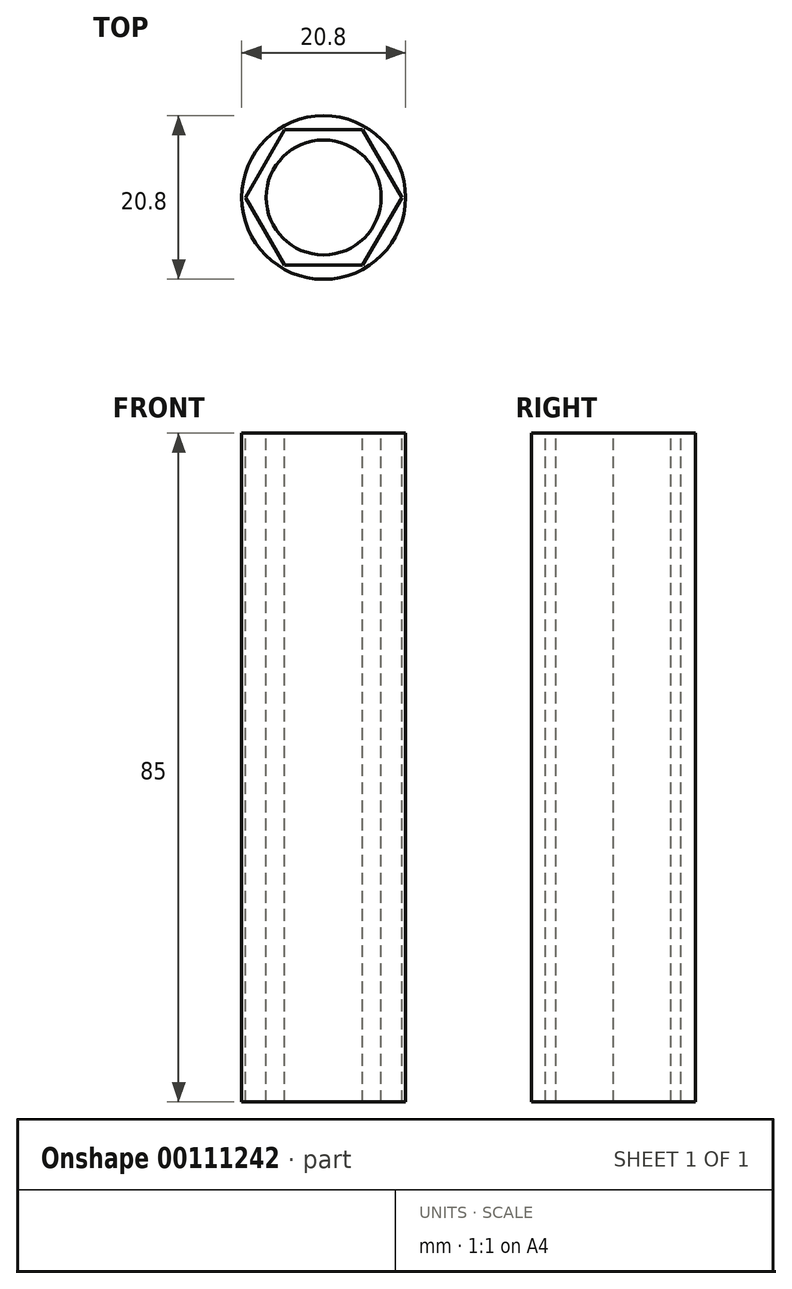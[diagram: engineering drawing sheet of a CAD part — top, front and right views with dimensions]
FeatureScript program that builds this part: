
annotation { "Feature Type Name" : "Feature", "Feature Type Description" : "" }
export const myFeature = defineFeature(function(context is Context, id is Id, definition is map)
    precondition{}
    {
        {
            var Q0;
            Q0=qCreatedBy(makeId("Top.planeOp"),FACE);
            var sketch = newSketch(context, id + "F0", { "sketchPlane" : qUnion([Q0])});
            skCircle(sketch, "E0.cCircle", {"center": v(0, 0) * mm, "radius": 8.6 * mm, "construction": true});
            skLineSegment(sketch, "E0.0", {"start": v(-4.97, 8.6) * mm, "end": v(4.97, 8.6) * mm});
            skLineSegment(sketch, "E0.1", {"start": v(4.97, 8.6) * mm, "end": v(9.93, 0) * mm});
            skLineSegment(sketch, "E0.2", {"start": v(9.93, 0) * mm, "end": v(4.97, -8.6) * mm});
            skLineSegment(sketch, "E0.3", {"start": v(4.97, -8.6) * mm, "end": v(-4.97, -8.6) * mm});
            skLineSegment(sketch, "E0.4", {"start": v(-4.97, -8.6) * mm, "end": v(-9.93, 0) * mm});
            skLineSegment(sketch, "E0.5", {"start": v(-9.93, 0) * mm, "end": v(-4.97, 8.6) * mm});
            skPoint(sketch, "E0.0.midPoint", {"position": v(0, 8.6) * mm});
            skSolve(sketch);
        }
        {
            var Q0;
            Q0=qCreatedBy(makeId("Top.planeOp"),FACE);
            var sketch = newSketch(context, id + "F1", { "sketchPlane" : qUnion([Q0])});
            skCircle(sketch, "E1", {"center": v(0, 0) * mm, "radius": 10.4 * mm});
            skSolve(sketch);
        }
        {
            var Q0;
            Q0=qCreatedBy(makeId("Top.planeOp"),FACE);
            var sketch = newSketch(context, id + "F2", { "sketchPlane" : qUnion([Q0])});
            skCircle(sketch, "E2", {"center": v(0, 0) * mm, "radius": 7.3 * mm});
            skSolve(sketch);
        }
        {
            var Q0;
            Q0=qCreatedBy(makeId("Top.planeOp"),FACE);
            cPlane(context, id + "F3", {"entities" : qUnion([Q0]), "cplaneType" : CPlaneType.OFFSET, "offset" : 85 * mm, "oppositeDirection" : true, "width" : 150 * mm, "height" : 150 * mm});
        }
        {
            var Q0;
            Q0 = qSketchRegion(id + "F0", true);
            var Q1;
            Q1=qCreatedBy(id+"F3.planeOp",FACE);
            extrude(context, id + "F4", {"entities" : qUnion([Q0]), "endBound" : BoundingType.UP_TO_SURFACE, "oppositeDirection" : true, "endBoundEntityFace" : qUnion([Q1]), "depth" : 25 * mm});
        }
        {
            var Q0;
            Q0 = qSketchRegion(id + "F1", true);
            var Q1;
            Q1=qCreatedBy(id+"F3.planeOp",FACE);
            extrude(context, id + "F5", {"entities" : qUnion([Q0]), "endBound" : BoundingType.UP_TO_SURFACE, "oppositeDirection" : true, "endBoundEntityFace" : qUnion([Q1]), "depth" : 25 * mm});
        }
        {
            var Q0;
            Q0 = qSketchRegion(id + "F2", true);
            var Q1;
            Q1=qCreatedBy(id+"F3.planeOp",FACE);
            extrude(context, id + "F6", {"entities" : qUnion([Q0]), "endBound" : BoundingType.UP_TO_SURFACE, "oppositeDirection" : true, "endBoundEntityFace" : qUnion([Q1]), "depth" : 25 * mm});
        }
    });
